# Revit family: Gira_216800
name_source: partatom
category: Electrical Fixtures
revit_build: Autodesk Revit 2017 (Build: 20160225_1515(x64)
units: mm (PartAtom-declared; Revit-internal decimal feet)

## family parameters
Cut with Voids When Loaded = No
Host = Face
Maintain Annotation Orientation = No
Part Type = Normal
Room Calculation Point = No
Round Connector Dimension = Use Diameter
Shared = No

## types (1)
- IP I/F KNX DRA
    BIM = https://media.live.bim.site X1 REG KNX.rfa
    BIMSITE_PRODUCT_ID = 0970236d5dbcfd86767d418a7bd093ba7f5cd1af
    Bus connection included = No
    Cost = 0 $
    Default Elevation = 1219 mm
    Description = IP I F DRA KNX KNX IP interface,DRA plus Features: - For coupling a PC to the KNX bus to address, program, or diagnose KNX components.,Notes : - Supply via external DC 24 V.
    GTIN = 4010337084457
    HAN = 216800
    HeinzeBIM = https://www.heinze.de
    Manufacturer = Gira
    Number of inputs = 0
    Radio frequent bidirectional = No
    Transparent = No
    URL = https://www.gira.de
    With label area = No

## geometry (parser evidence)
native form markers: Blend x2, Sweep x3
no freeform markers — native parametric forms only
